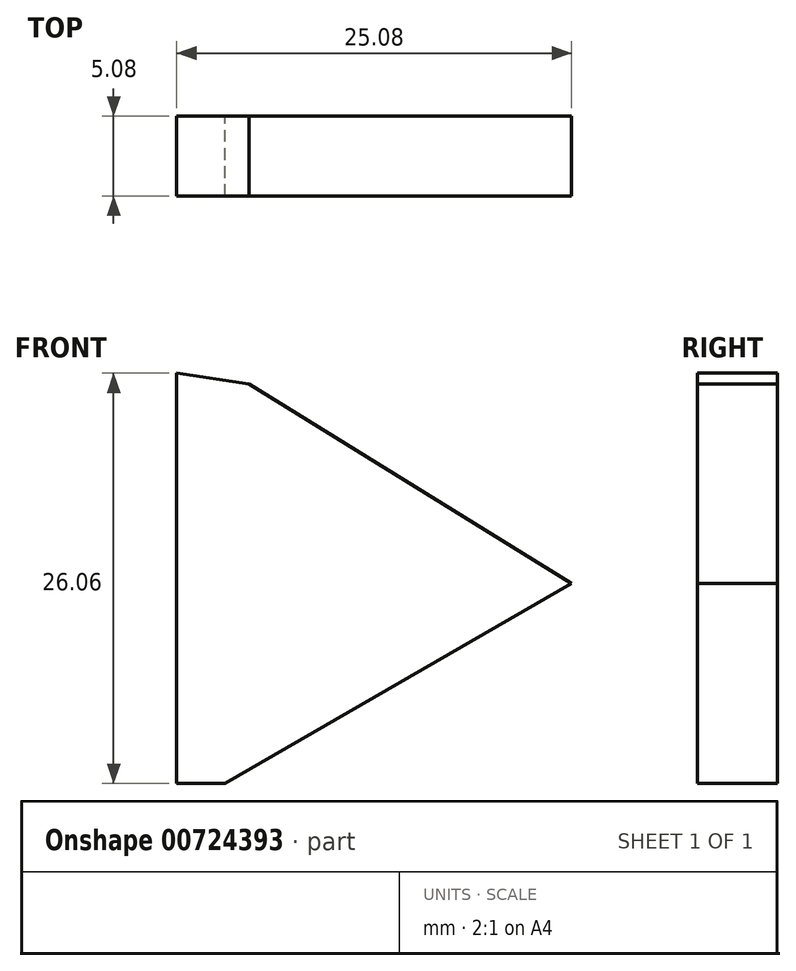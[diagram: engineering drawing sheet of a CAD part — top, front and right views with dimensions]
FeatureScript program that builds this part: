
annotation { "Feature Type Name" : "Feature", "Feature Type Description" : "" }
export const myFeature = defineFeature(function(context is Context, id is Id, definition is map)
    precondition{}
    {
        {
            var Q0;
            Q0=qCreatedBy(makeId("Front.planeOp"),FACE);
            var sketch = newSketch(context, id + "F0", { "sketchPlane" : qUnion([Q0])});
            skLineSegment(sketch, "E0", {"start": v(0, 0) * mm, "end": v(0, 13.36) * mm});
            skLineSegment(sketch, "E1", {"start": v(0, 0) * mm, "end": v(0, -12.7) * mm});
            skLineSegment(sketch, "E2", {"start": v(3.49, 13.36) * mm, "end": v(25.08, 0) * mm});
            skLineSegment(sketch, "E3", {"start": v(3.09, -12.7) * mm, "end": v(25.08, 0) * mm});
            skLineSegment(sketch, "E4", {"start": v(3.09, -12.7) * mm, "end": v(0, -12.7) * mm});
            skLineSegment(sketch, "E5", {"start": v(4.58, 12.69) * mm, "end": v(0, 13.36) * mm});
            skSolve(sketch);
        }
        {
            var Q0;
            Q0 = qSketchRegion(id + "F0", true);
            extrude(context, id + "F1", {"entities" : qUnion([Q0]), "depth" : 5.08 * mm, "offsetDistance" : 25.4 * mm});
        }
    });
